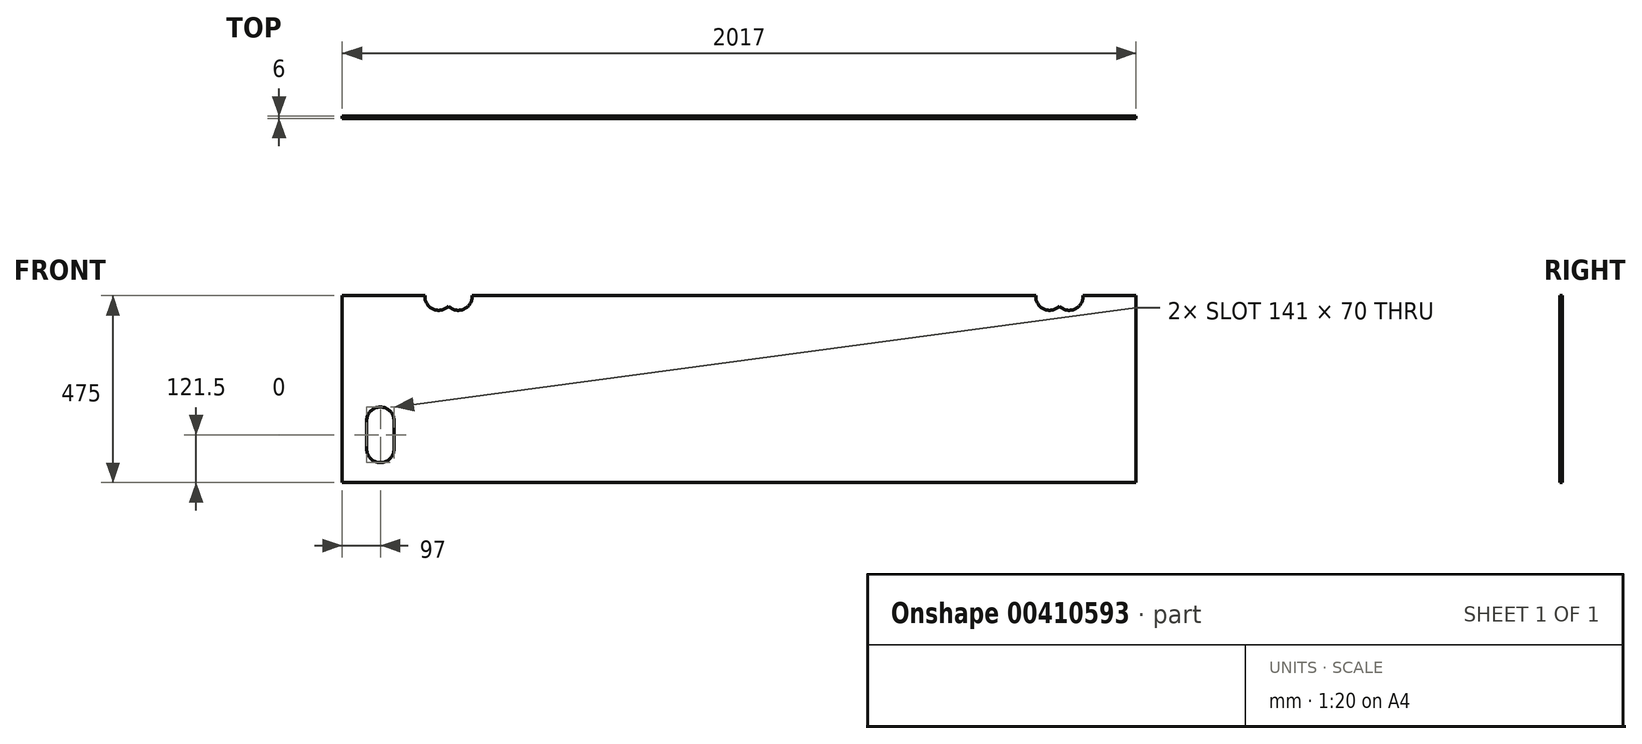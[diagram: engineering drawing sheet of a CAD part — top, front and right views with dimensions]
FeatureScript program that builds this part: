
annotation { "Feature Type Name" : "Feature", "Feature Type Description" : "" }
export const myFeature = defineFeature(function(context is Context, id is Id, definition is map)
    precondition{}
    {
        {
            var Q0;
            Q0=qCreatedBy(makeId("Front.planeOp"),FACE);
            var sketch = newSketch(context, id + "F0", { "sketchPlane" : qUnion([Q0])});
            skLineSegment(sketch, "E0.bottom", {"start": v(0, 0) * mm, "end": v(2017, 0) * mm});
            skLineSegment(sketch, "E0.top", {"start": v(0, 475) * mm, "end": v(210.06, 475) * mm});
            skLineSegment(sketch, "E0.left", {"start": v(0, 0) * mm, "end": v(0, 475) * mm});
            skLineSegment(sketch, "E0.right", {"start": v(2017, 0) * mm, "end": v(2017, 475) * mm});
            skLineSegment(sketch, "E1", {"start": v(97, 225.87) * mm, "end": v(97, 41.27) * mm, "construction": true});
            skArc(sketch, "E2", {"start": v(132, 157) * mm, "mid": v(97, 192) * mm, "end": v(62, 157) * mm});
            skLineSegment(sketch, "E3", {"start": v(132, 157) * mm, "end": v(132, 86) * mm});
            skLineSegment(sketch, "E4", {"start": v(62, 157) * mm, "end": v(62, 86) * mm});
            skArc(sketch, "E5.trimOffspring", {"start": v(62, 86) * mm, "mid": v(97, 51) * mm, "end": v(132, 86) * mm});
            skArc(sketch, "E6", {"start": v(235.06, 475) * mm, "mid": v(270, 438) * mm, "end": v(304.94, 475) * mm, "construction": true});
            skLineSegment(sketch, "E7", {"start": v(270, 473) * mm, "end": v(270, 343.62) * mm, "construction": true});
            skCircle(sketch, "E8", {"center": v(295, 442) * mm, "radius": 2.5 * mm, "construction": true});
            skLineSegment(sketch, "E9.trimOffspring", {"start": v(329.94, 475) * mm, "end": v(1762.06, 475) * mm});
            skLineSegment(sketch, "E10", {"start": v(1822, 577.57) * mm, "end": v(1822, 322.48) * mm, "construction": true});
            skLineSegment(sketch, "E11.trimOffspring", {"start": v(1881.94, 475) * mm, "end": v(2017, 475) * mm});
            skLineSegment(sketch, "E12", {"start": v(-379.25, -3) * mm, "end": v(2247, -3) * mm, "construction": true});
            skLineSegment(sketch, "E13", {"start": v(-346.74, 476.48) * mm, "end": v(2292.46, 480.4) * mm, "construction": true});
            skPoint(sketch, "E14", {"position": v(1822, 479.7) * mm});
            skLineSegment(sketch, "E15", {"start": v(214.18, 473) * mm, "end": v(350.67, 473) * mm, "construction": true});
            skArc(sketch, "E16", {"start": v(270, 448.5) * mm, "mid": v(309.15, 440.99) * mm, "end": v(329.94, 475) * mm});
            skLineSegment(sketch, "E17", {"start": v(295, 442) * mm, "end": v(295, 499.8) * mm, "construction": true});
            skArc(sketch, "E18.MirrorCS", {"start": v(270, 448.5) * mm, "mid": v(230.85, 440.99) * mm, "end": v(210.06, 475) * mm});
            skCircle(sketch, "E19", {"center": v(245, 442) * mm, "radius": 2.5 * mm, "construction": true});
            skLineSegment(sketch, "E20", {"start": v(1724.05, 473) * mm, "end": v(1935.44, 473) * mm, "construction": true});
            skLineSegment(sketch, "E21", {"start": v(1847, 494.06) * mm, "end": v(1847, 395.8) * mm, "construction": true});
            skLineSegment(sketch, "E22", {"start": v(1797, 493.4) * mm, "end": v(1797, 389.98) * mm, "construction": true});
            skArc(sketch, "E23", {"start": v(1822, 448.5) * mm, "mid": v(1861.15, 440.99) * mm, "end": v(1881.94, 475) * mm});
            skArc(sketch, "E24.MirrorCS", {"start": v(1822, 448.5) * mm, "mid": v(1782.85, 440.99) * mm, "end": v(1762.06, 475) * mm});
            skSolve(sketch);
        }
        {
            var Q0;
            Q0=makeQuery(id+"F0.imprint","IMPRINT",FACE,{"disambiguationData":[TD([[makeQuery(id+"F0.imprint","IMPRINT",EDGE,{"derivedFrom":sQuery(id+"F0.wireOp",EDGE,"E0.bottom")}),1.0]])]});
            extrude(context, id + "F1", {"entities" : qUnion([Q0]), "depth" : 6 * mm});
        }
    });
